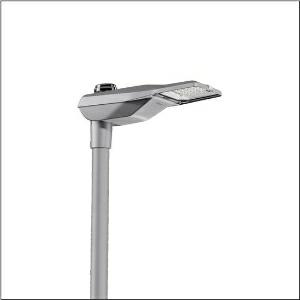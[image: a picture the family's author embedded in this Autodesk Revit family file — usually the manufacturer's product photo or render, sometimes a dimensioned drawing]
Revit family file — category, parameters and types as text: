
# Revit family: streetlight_sl_21_micro___stw1_0a_5xe5e47n08cb_41ee
name_source: partatom
category: Lighting Fixtures
units: mm (PartAtom-declared; Revit-internal decimal feet)

## family parameters
Cut with Voids When Loaded = No
Host = Face
Light Source = No
Part Type = Normal
Room Calculation Point = No
Round Connector Dimension = Use Diameter
Shared = No

## types (1)
- --- (1 x LED, 2380 lm, 15.8 W, 4000K)
    Apparent Load = 16 VA
    CIE Flux Codes = 38 75 98 100 100
    Color Rendering = 70
    Color Temperature = 4000K
    Default Elevation = 1800 mm
    Description = Streetlight SL 21 micro, mast luminaire, primary light control with lens, of PMMA, primary optical cover: cover, of toughened safety glass, transparent, light distribution: STW1.0a, light emission: direct distribution, primary light characteristic: asymmetric, installation type: post-top, LED, 3G 1.5mm², High Power LED, rated luminous flux: 2.380lm, luminous efficacy: 151lm/W, light colour: 740, colour temperature: 4000K, control gear: NEMA (7pin), control: overheat protection, pre-setting: linear dimming characteristic, constant luminous flux control, time-dependent luminous flux control, flexible luminous flux parameterisation, mains connection: 230..240V, AC, 50/60Hz, connection cable pre-assembled, cable length: 6,5m, wiring characteristics: H07RN-F, start of lifetime: 16W, end of service life: 16W, reduction: 8W, luminaire housing, of diecast aluminium (EN AC-44300), powder-coated, Siteco® metallic grey (DB 702S), corrosivity category C5 mid according to DIN EN ISO 12944, multi-level sealing system, sealing non-destructively replaceable, inclination adjustable: 0°, 5°, 10°, 15°, length: 528mm, width: 235mm, height: 110mm, spigot size: 76/60mm (post-top), mounting height: 4..8m, protection rating (complete): IP66, insulation class (complete): insulation class I (protective earthing), certification: CE, ENEC, ENEC+, VDE, impact resistance: IK10, permissible operating ambient temperature for outdoor applications: -40..+50°C, standard-compliant lighting for roads and squares, packaging unit: 1 piece

Light Distribution: STW1.0a
    Height = 110 mm
    Lamp = 1 x LED
    Lamp Light Flux = 2380 lm
    Lamp Power = 15.8 W
    Lamp count = 1
    Length = 528 mm
    Luminous efficacy = 151 lm/W
    Manufacturer = Siteco
    ModVariant = No
    Model = 5XE5E47N08CB
    Number of Poles = 1
    OnlyDefault = Yes
    Power Factor = 1
    Product Name = Streetlight SL 21 micro | STW1.0a
    Product group = mast luminaire | pylon top
    ProductGroupID = 6100
    Protection Class = Protection class I
    Protection Degree = IP 66
    RLX_Detail_Level = 1
    RLX_Emergency_Light_Flux = 0 lm
    RLX_Emergency_Type = 0
    RLX_Emergency_Type_DB = No
    RlxData = <blob elided: 98077 chars, md5=db5a0057>
    Socket = socket
    Standby Power = 0 W
    System Light Flux = 2380 lm
    System Power = 16 W
    Type Comments = factory setting: luminous flux: 100 % | dim-lin: 254 | 300 mA
    Type Image = l_1294375.jpg
    URL = http://relux.com
    VarID = @adj_157271
    Voltage = 0 V
    Weight = 0.00 kg
    Width = 235 mm

## geometry (parser evidence)
native form markers: Blend x4, Sweep x9
no freeform markers — native parametric forms only
